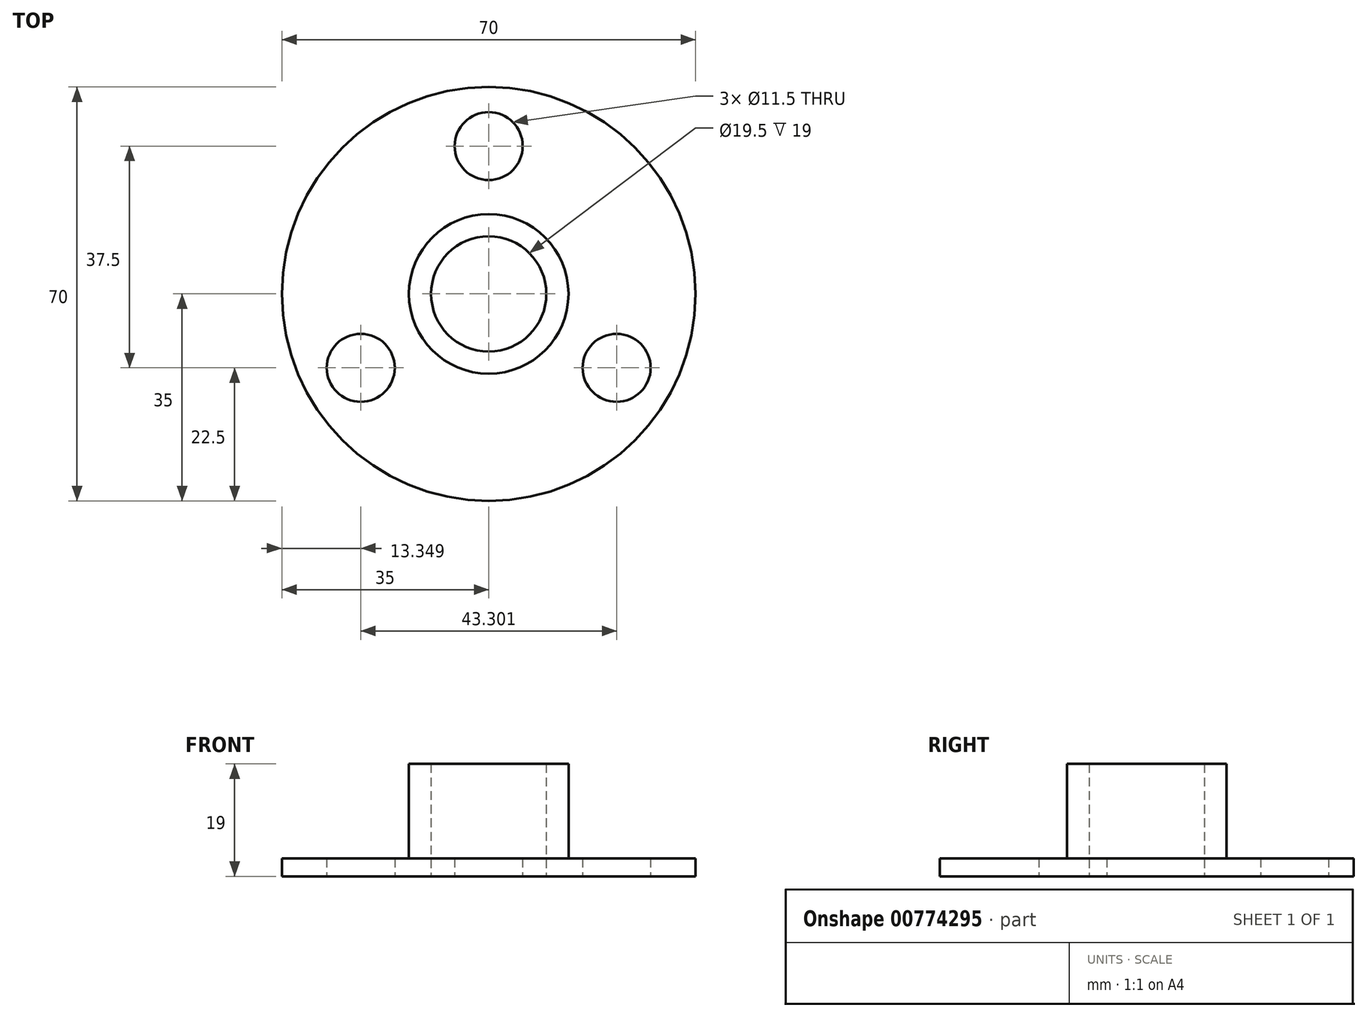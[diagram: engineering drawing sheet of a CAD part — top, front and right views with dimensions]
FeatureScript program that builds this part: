
annotation { "Feature Type Name" : "Feature", "Feature Type Description" : "" }
export const myFeature = defineFeature(function(context is Context, id is Id, definition is map)
    precondition{}
    {
        {
            var Q0;
            Q0=qCreatedBy(makeId("Top.planeOp"),FACE);
            var sketch = newSketch(context, id + "F0", { "sketchPlane" : qUnion([Q0])});
            skCircle(sketch, "E0", {"center": v(0, 0) * mm, "radius": 9.75 * mm});
            skCircle(sketch, "E1", {"center": v(0, 0) * mm, "radius": 13.5 * mm});
            skCircle(sketch, "E2", {"center": v(0, 0) * mm, "radius": 17.5 * mm, "construction": true});
            skCircle(sketch, "E3", {"center": v(0, 0) * mm, "radius": 35 * mm});
            skCircle(sketch, "E4.1.0", {"center": v(0, 25) * mm, "radius": 5.75 * mm});
            skPoint(sketch, "E4.center", {"position": v(15, 0) * mm});
            skCircle(sketch, "E5.1.0", {"center": v(-21.65, -12.5) * mm, "radius": 5.75 * mm});
            skCircle(sketch, "E5.2.0", {"center": v(21.65, -12.5) * mm, "radius": 5.75 * mm});
            skSolve(sketch);
        }
        {
            var Q0;
            Q0=makeQuery(id+"F0.imprint","IMPRINT",FACE,{"disambiguationData":[TD([[makeQuery(id+"F0.imprint","IMPRINT",EDGE,{"derivedFrom":sQuery(id+"F0.wireOp",EDGE,"E1")}),-1.0]])]});
            extrude(context, id + "F1", {"entities" : qUnion([Q0]), "depth" : 3 * mm, "offsetDistance" : 25 * mm});
        }
        {
            var Q0;
            Q0=makeQuery(id+"F0.imprint","IMPRINT",FACE,{"disambiguationData":[TD([[makeQuery(id+"F0.imprint","IMPRINT",EDGE,{"derivedFrom":sQuery(id+"F0.wireOp",EDGE,"E0")}),-1.0]])]});
            extrude(context, id + "F2", {"entities" : qUnion([Q0]), "operationType" : NewBodyOperationType.ADD, "depth" : 19 * mm, "offsetDistance" : 25 * mm});
        }
    });
